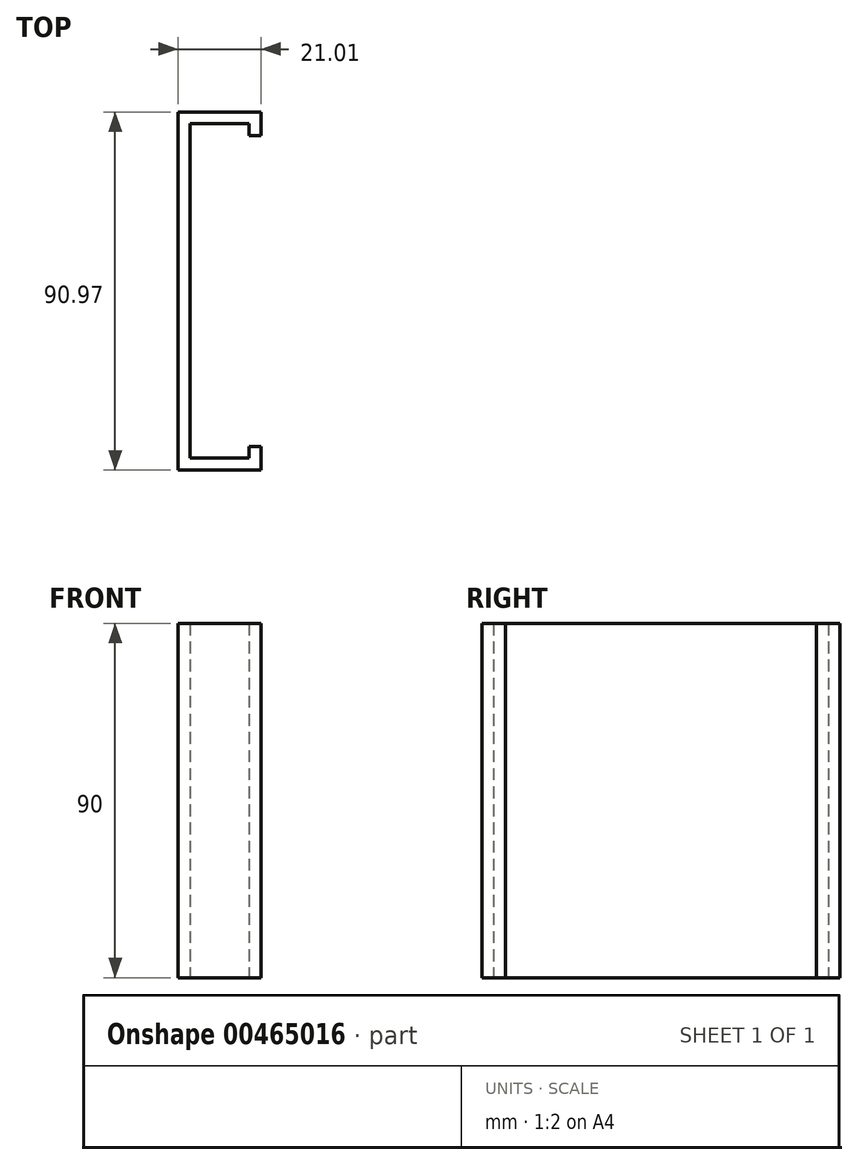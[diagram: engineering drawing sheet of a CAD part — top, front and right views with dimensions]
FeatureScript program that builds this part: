
annotation { "Feature Type Name" : "Feature", "Feature Type Description" : "" }
export const myFeature = defineFeature(function(context is Context, id is Id, definition is map)
    precondition{}
    {
        {
            var Q0;
            Q0=qCreatedBy(makeId("Top.planeOp"),FACE);
            var sketch = newSketch(context, id + "F0", { "sketchPlane" : qUnion([Q0])});
            skLineSegment(sketch, "E0", {"start": v(-47.42, -62.26) * mm, "end": v(-47.42, 22.74) * mm});
            skLineSegment(sketch, "E1", {"start": v(-47.42, 22.74) * mm, "end": v(-32.42, 22.74) * mm});
            skLineSegment(sketch, "E2", {"start": v(-29.79, 25.71) * mm, "end": v(-47.42, 25.71) * mm});
            skLineSegment(sketch, "E3", {"start": v(-47.42, 25.71) * mm, "end": v(-50.42, 25.71) * mm});
            skLineSegment(sketch, "E4", {"start": v(-50.42, 25.71) * mm, "end": v(-50.42, -62.26) * mm});
            skLineSegment(sketch, "E5", {"start": v(-50.42, -62.26) * mm, "end": v(-50.42, -65.26) * mm});
            skLineSegment(sketch, "E6", {"start": v(-47.42, -62.26) * mm, "end": v(-32.41, -62.26) * mm});
            skLineSegment(sketch, "E7", {"start": v(-32.41, -62.26) * mm, "end": v(-32.41, -59.26) * mm});
            skLineSegment(sketch, "E8", {"start": v(-32.41, -59.26) * mm, "end": v(-29.41, -59.26) * mm});
            skLineSegment(sketch, "E9", {"start": v(-29.41, -59.26) * mm, "end": v(-29.41, -65.26) * mm});
            skLineSegment(sketch, "E10", {"start": v(-29.41, -65.26) * mm, "end": v(-50.42, -65.26) * mm});
            skLineSegment(sketch, "E11", {"start": v(-32.42, 22.74) * mm, "end": v(-32.42, 19.74) * mm});
            skLineSegment(sketch, "E12", {"start": v(-32.42, 19.74) * mm, "end": v(-29.42, 19.74) * mm});
            skLineSegment(sketch, "E13", {"start": v(-29.42, 19.74) * mm, "end": v(-29.42, 25.71) * mm});
            skLineSegment(sketch, "E14", {"start": v(-29.42, 25.71) * mm, "end": v(-29.79, 25.71) * mm});
            skSolve(sketch);
        }
        {
            var Q0;
            Q0=makeQuery(id+"F0.imprint","IMPRINT",FACE,{"disambiguationData":[TD([[makeQuery(id+"F0.imprint","IMPRINT",EDGE,{"derivedFrom":sQuery(id+"F0.wireOp",EDGE,"E0")}),1.0]])]});
            extrude(context, id + "F1", {"entities" : qUnion([Q0]), "depth" : 90 * mm});
        }
    });
